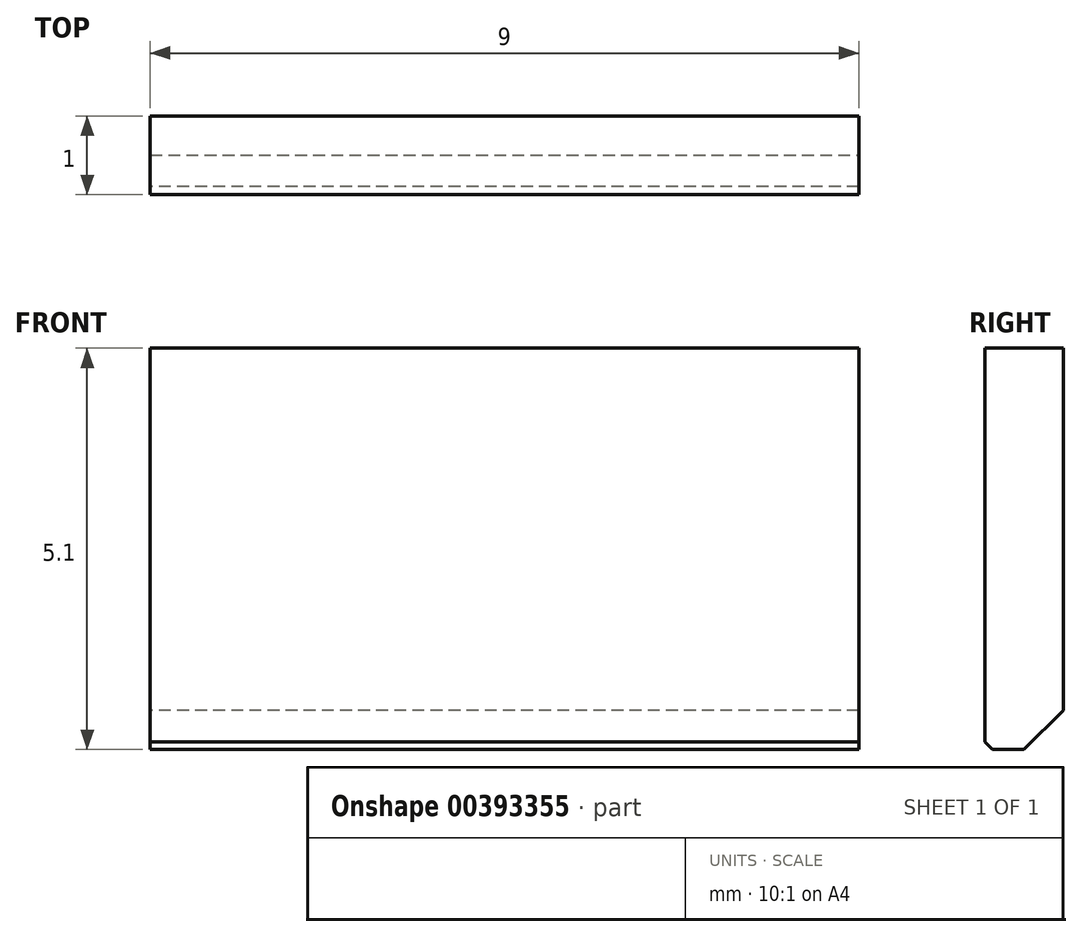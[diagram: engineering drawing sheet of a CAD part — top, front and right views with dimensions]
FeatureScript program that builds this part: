
annotation { "Feature Type Name" : "Feature", "Feature Type Description" : "" }
export const myFeature = defineFeature(function(context is Context, id is Id, definition is map)
    precondition{}
    {
        {
            var Q0;
            Q0=qCreatedBy(makeId("Front.planeOp"),FACE);
            var sketch = newSketch(context, id + "F0", { "sketchPlane" : qUnion([Q0])});
            skLineSegment(sketch, "E0.bottom", {"start": v(0, 0) * mm, "end": v(9, 0) * mm});
            skLineSegment(sketch, "E0.top", {"start": v(0, 5.1) * mm, "end": v(9, 5.1) * mm});
            skLineSegment(sketch, "E0.left", {"start": v(0, 0) * mm, "end": v(0, 5.1) * mm});
            skLineSegment(sketch, "E0.right", {"start": v(9, 0) * mm, "end": v(9, 5.1) * mm});
            skSolve(sketch);
        }
        {
            var Q0;
            Q0 = qSketchRegion(id + "F0", true);
            var Q1;
            Q1=makeQuery(id+"F0.imprint","IMPRINT",FACE,{"disambiguationData":[TD([[makeQuery(id+"F0.imprint","IMPRINT",EDGE,{"derivedFrom":sQuery(id+"F0.wireOp",EDGE,"E0.bottom")}),1.0]])]});
            extrude(context, id + "F1", {"entities" : qUnion([Q0, Q1]), "endBound" : BoundingType.SYMMETRIC, "depth" : 1 * mm});
        }
        {
            var Q0;
            Q0=makeQuery(id+"F1.opExtrude","CAP_EDGE",EDGE,{"disambiguationData":[OSD([sQuery(id+"F0.wireOp",EDGE,"E0.bottom")])],"isStart":true});
            chamfer(context, id + "F2", {"entities" : qUnion([Q0]), "width" : 0.5 * mm, "tangentPropagation" : true});
        }
        {
            var Q0;
            Q0=makeQuery(id+"F1.opExtrude","CAP_EDGE",EDGE,{"disambiguationData":[OSD([sQuery(id+"F0.wireOp",EDGE,"E0.bottom")])],"isStart":false});
            chamfer(context, id + "F3", {"entities" : qUnion([Q0]), "width" : 0.1 * mm, "tangentPropagation" : true});
        }
    });
